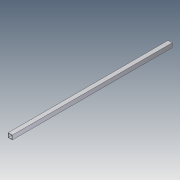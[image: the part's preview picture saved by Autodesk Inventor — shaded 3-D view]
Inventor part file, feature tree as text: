
AUTODESK INVENTOR PART (.ipt)
format: ipt  version: 2012 (Build 160160000, 160)  size: 71,680 bytes
history: native  units: in
note: dims shown in document units (in); Inventor stores cm internally (conversion verified against a paired STEP export)
features: extrude x1, sketch x1
ambient origin geometry x8: Origin, YZ Plane, XZ Plane, XY Plane, X Axis, Y Axis, Z Axis, Center Point
bodies: Solid1 (feature_tree)
feature tree (2):
  extrude  "Extrusion1"  Depth=0.125in
  sketch  "Sketch1"  dims[d0=1.25in d1=0.125in d2=47.75in d3=0.0in]
